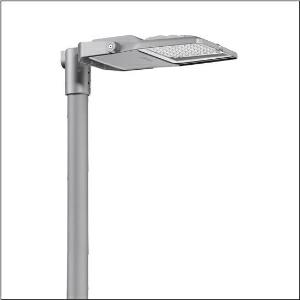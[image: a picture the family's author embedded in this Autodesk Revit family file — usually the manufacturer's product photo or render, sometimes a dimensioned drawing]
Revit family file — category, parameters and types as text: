
# Revit family: floodlight_fl_21_iq_mini___pl33t_5xa7772c2f3a_076b
name_source: partatom
category: Lighting Fixtures
units: mm (PartAtom-declared; Revit-internal decimal feet)

## family parameters
Cut with Voids When Loaded = No
Host = Face
Light Source = No
Part Type = Normal
Room Calculation Point = No
Round Connector Dimension = Use Diameter
Shared = No

## types (1)
- --- (1 x LED, 12060 lm, 87.2 W, 3000K)
    Apparent Load = 87 VA
    CIE Flux Codes = 26 75 99 100 100
    Color Rendering = 70
    Color Temperature = 3000K
    Default Elevation = 1800 mm
    Description = Floodlight FL 21 iQ mini, floodlight, primary light control with lens, of PMMA, primary optical cover: protective disc, of toughened safety glass, transparent, light distribution: PL33T, light emission: direct distribution, installation type: surface-mounted, LED, High Power LED, rated luminous flux: 12.060lm, luminous efficacy: 138lm/W, light colour: 730, colour temperature: 3000K, control: Auto-Match, Temp-Guard, Night-Set, Smart-Wire, Desk-Remote (wireless, voltage-free reading and setting of iQ features in the workshop via application-optimized NFC function/RFID function), optimised constant luminous flux control (CLO 2.0), Light-Fading, Lumen-Switch, with terminal, 6-pole, mains connection: 220..240V, AC, 50/60Hz, start of lifetime: 87W, end of service life: 92W, reduction: 40W, luminaire housing, of diecast aluminium, powder-coated, Siteco® metallic grey (DB 702S), corrosivity category C5 mid according to DIN EN ISO 12944, sealing non-destructively replaceable, please order mast flange separately, mast bracket, of steel, galvanised, powder-coated, protection rating (complete): IP66, insulation class (complete): insulation class II (safety insulation), certification: CE, ENEC, VDE, protection symbol: D, impact resistance: IK08, permissible operating ambient temperature: -40..+40°C, permissible operating ambient temperature for outdoor applications: -40..+50°C, standard: DIN EN 12944, LABS conformity tested according to VDMA 24364:2018-05, packaging unit: 1 piece

Light Distribution: PL33T
    Height = 70 mm
    Lamp = 1 x LED
    Lamp Light Flux = 12060 lm
    Lamp Power = 87.2 W
    Lamp count = 1
    Length = 485 mm
    Luminous efficacy = 138 lm/W
    Manufacturer = Siteco
    ModVariant = No
    Model = 5XA7772C2F3A
    Number of Poles = 1
    OnlyDefault = Yes
    Power Factor = 1
    Product Name = Floodlight FL 21 iQ mini | PL33T
    Product group = floodlight | pylon annexe
    ProductGroupID = 6200
    Protection Class = Protection class II
    Protection Degree = IP 66
    RLX_Detail_Level = 1
    RLX_Emergency_Light_Flux = 0 lm
    RLX_Emergency_Type = 0
    RLX_Emergency_Type_DB = No
    RlxData = <blob elided: 101217 chars, md5=84002f17>
    Socket = socket
    Standby Power = 0 W
    System Light Flux = 12060 lm
    System Power = 87 W
    Type Comments = factory setting: luminous flux: 100 % | dim-lin: 254 | 456 mA
    Type Image = l_1007125.jpg
    URL = http://relux.com
    VarID = @adj_099649
    Voltage = 0 V
    Weight = 0.00 kg
    Width = 337 mm

## geometry (parser evidence)
native form markers: Blend x4, Sweep x13
no freeform markers — native parametric forms only
